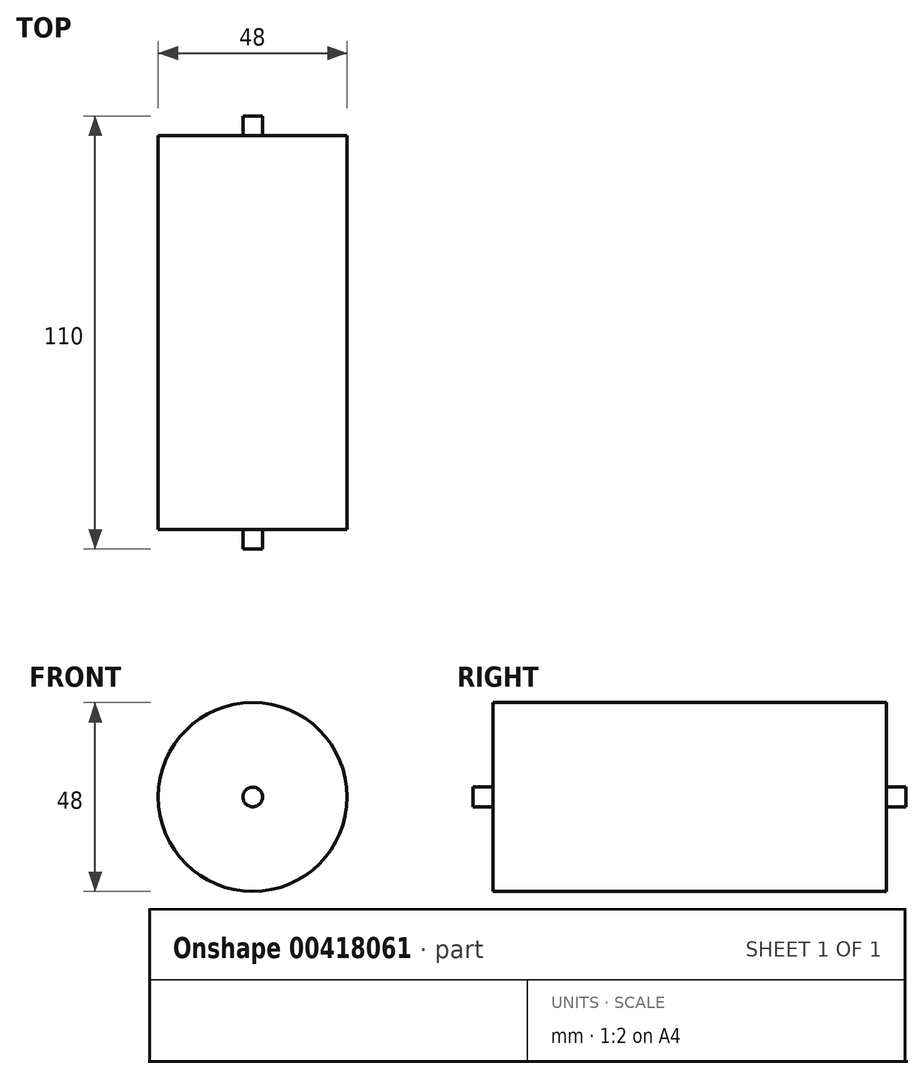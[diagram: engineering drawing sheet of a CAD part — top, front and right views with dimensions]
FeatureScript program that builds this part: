
annotation { "Feature Type Name" : "Feature", "Feature Type Description" : "" }
export const myFeature = defineFeature(function(context is Context, id is Id, definition is map)
    precondition{}
    {
        {
            var Q0;
            Q0=qCreatedBy(makeId("Front.planeOp"),FACE);
            var sketch = newSketch(context, id + "F0", { "sketchPlane" : qUnion([Q0])});
            skCircle(sketch, "E0", {"center": v(0, 0) * mm, "radius": 24 * mm});
            skSolve(sketch);
        }
        {
            var Q0;
            Q0 = qSketchRegion(id + "F0", true);
            extrude(context, id + "F1", {"entities" : qUnion([Q0]), "depth" : 100 * mm, "offsetDistance" : 25 * mm});
        }
        {
            var Q0;
            Q0=makeQuery(id+"F1.opExtrude","CAP_FACE",FACE,{"disambiguationData":[OSD([sQuery(id+"F0.wireOp",EDGE,"E0")])],"isStart":false});
            var sketch = newSketch(context, id + "F2", { "sketchPlane" : qUnion([Q0])});
            skCircle(sketch, "E1", {"center": v(0, 0) * mm, "radius": 2.5 * mm});
            skSolve(sketch);
        }
        {
            var Q0;
            Q0 = qSketchRegion(id + "F2", true);
            extrude(context, id + "F3", {"entities" : qUnion([Q0]), "operationType" : NewBodyOperationType.ADD, "depth" : 5 * mm, "offsetDistance" : 25 * mm});
        }
        {
            var Q0;
            Q0=makeQuery(id+"F1.opExtrude","CAP_FACE",FACE,{"disambiguationData":[OSD([sQuery(id+"F0.wireOp",EDGE,"E0")])],"isStart":true});
            var sketch = newSketch(context, id + "F4", { "sketchPlane" : qUnion([Q0])});
            skCircle(sketch, "E2", {"center": v(0, 0) * mm, "radius": 2.5 * mm});
            skSolve(sketch);
        }
        {
            var Q0;
            Q0 = qSketchRegion(id + "F4", true);
            extrude(context, id + "F5", {"entities" : qUnion([Q0]), "operationType" : NewBodyOperationType.ADD, "depth" : 5 * mm, "offsetDistance" : 25 * mm});
        }
    });
